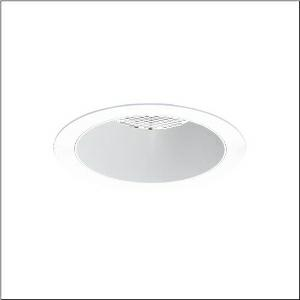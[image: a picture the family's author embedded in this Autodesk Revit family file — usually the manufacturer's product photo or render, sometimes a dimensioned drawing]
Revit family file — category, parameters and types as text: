
# Revit family: lunis_21_xl_51db18mf91c
name_source: partatom
category: Lighting Fixtures
units: mm (PartAtom-declared; Revit-internal decimal feet)

## family parameters
Cut with Voids When Loaded = No
Host = Face
Light Source = No
Part Type = Normal
Room Calculation Point = No
Round Connector Dimension = Use Diameter
Shared = No

## types (1)
- --- (1 x LED, 3700 lm, 21.7 W, 6500K)
    Apparent Load = 22 VA
    CIE Flux Codes = 87 97 99 100 100
    Color Rendering = 80
    Color Temperature = 6500K
    Default Elevation = 1800 mm
    Description = Lunis 21 XL, downlight, light control with lens, of PMMA, anti glare with reflector, of PC, light emission: direct distribution, LED rated luminous flux: 2.480lm, light colour: 830/840/865, with terminal, 3-pole, mains connection: 220..240V, AC/DC, 0/50..60Hz, housing, round, of diecast aluminium, traffic white (RAL 9016), diameter: 230mm, clamping range: 1..40mm, protection rating (complete): IP20, protection rating (on room side): IP54, insulation class (complete): insulation class II (safety insulation), certification: CE, impact resistance: IK03, packaging unit: 1 piece
    Height = 0 mm  [stored 0 ft]
    Lamp = 1 x LED
    Lamp Light Flux = 3700 lm
    Lamp Power = 21.7 W
    Lamp count = 1
    Length = 230 mm
    Luminous efficacy = 171 lm/W
    Manufacturer = Siteco
    ModVariant = No
    Model = 51DB18MF91C
    Mounting Place = Ceiling
    Mounting Type = Recessed
    Number of Poles = 1
    OnlyDefault = Yes
    Power Factor = 1
    Product Name = Lunis 21 XL
    Product group = downlight
    ProductGroupID = 401
    Protection Class = Protection class II
    Protection Degree = IP 20
    RLX_Detail_Level = 1
    RLX_Emergency_Light_Flux = 0 lm
    RLX_Emergency_Type = 0
    RLX_Emergency_Type_DB = No
    RlxData = <blob elided: 18281 chars, md5=15581437>
    Socket = socket
    Standby Power = 0 W
    System Light Flux = 3700 lm
    System Power = 22 W
    Type Comments = individual setting: colour temperature 6500K, luminous flux: 100 % | (OFF | ON | ON | ON) | 650 mA
    Type Image = l_1291159.jpg
    URL = http://relux.com
    VarID = @adj_035167
    Voltage = 0 V
    Weight = 0.00 kg
    Width = 0 mm  [stored 0 ft]

note: [stored X ft] marks values corroborated as IEEE doubles in the binary element streams (Revit-internal decimal feet)

## geometry (parser evidence)
native form markers: Blend x4, Sweep x11
no freeform markers — native parametric forms only
